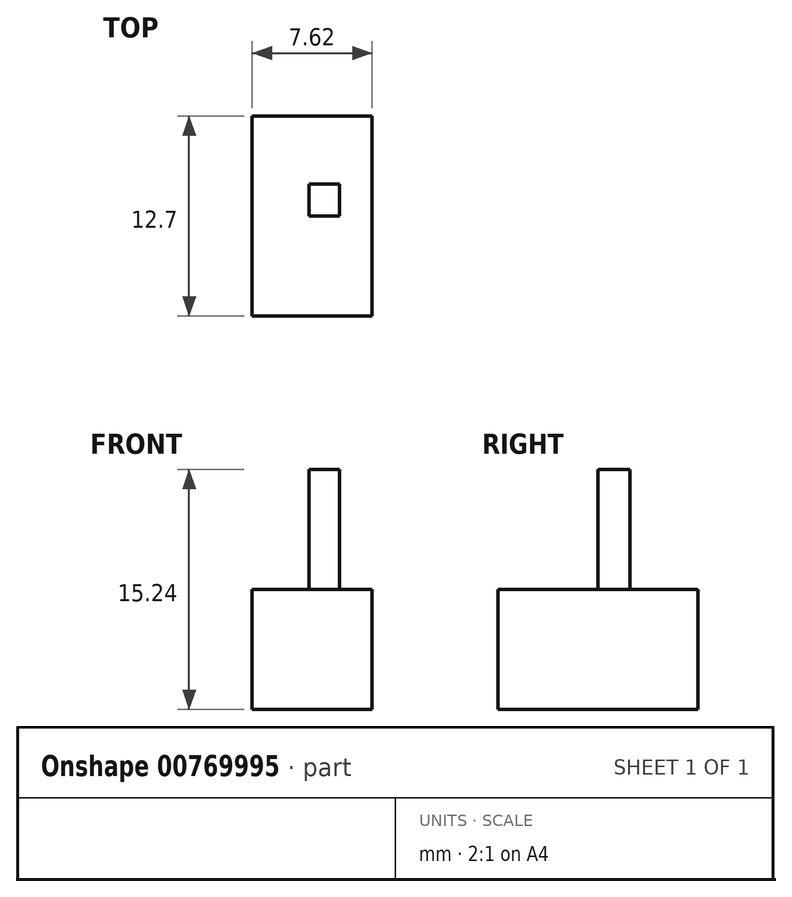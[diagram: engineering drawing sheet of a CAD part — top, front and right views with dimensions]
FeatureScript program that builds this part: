
annotation { "Feature Type Name" : "Feature", "Feature Type Description" : "" }
export const myFeature = defineFeature(function(context is Context, id is Id, definition is map)
    precondition{}
    {
        {
            var Q0;
            Q0=qCreatedBy(makeId("Top.planeOp"),FACE);
            var sketch = newSketch(context, id + "F0", { "sketchPlane" : qUnion([Q0])});
            skLineSegment(sketch, "E0.bottom", {"start": v(-56.96, -32.9) * mm, "end": v(-49.34, -32.9) * mm});
            skLineSegment(sketch, "E0.top", {"start": v(-56.96, -45.6) * mm, "end": v(-49.34, -45.6) * mm});
            skLineSegment(sketch, "E0.left", {"start": v(-56.96, -32.9) * mm, "end": v(-56.96, -45.6) * mm});
            skLineSegment(sketch, "E0.right", {"start": v(-49.34, -32.9) * mm, "end": v(-49.34, -45.6) * mm});
            skSolve(sketch);
        }
        {
            var Q0;
            Q0 = qSketchRegion(id + "F0", true);
            extrude(context, id + "F1", {"entities" : qUnion([Q0]), "depth" : 7.62 * mm, "offsetDistance" : 25.4 * mm});
        }
        {
            var Q0;
            Q0=makeQuery(id+"F1.opExtrude","CAP_FACE",FACE,{"disambiguationData":[OSD([sQuery(id+"F0.wireOp",EDGE,"E0.bottom"),sQuery(id+"F0.wireOp",EDGE,"E0.top"),sQuery(id+"F0.wireOp",EDGE,"E0.left"),sQuery(id+"F0.wireOp",EDGE,"E0.right")])],"isStart":false});
            var sketch = newSketch(context, id + "F2", { "sketchPlane" : qUnion([Q0])});
            skPoint(sketch, "E1.oppositeSnap0", {"position": v(-49.34, -39.25) * mm});
            skLineSegment(sketch, "E1.bottom", {"start": v(-53.34, -37.21) * mm, "end": v(-51.42, -37.21) * mm});
            skLineSegment(sketch, "E1.top", {"start": v(-53.34, -39.25) * mm, "end": v(-51.42, -39.25) * mm});
            skLineSegment(sketch, "E1.left", {"start": v(-53.34, -37.21) * mm, "end": v(-53.34, -39.25) * mm});
            skLineSegment(sketch, "E1.right", {"start": v(-51.42, -37.21) * mm, "end": v(-51.42, -39.25) * mm});
            skSolve(sketch);
        }
        {
            var Q0;
            Q0=makeQuery(id+"F2.imprint","IMPRINT",FACE,{"disambiguationData":[TD([[makeQuery(id+"F2.imprint","IMPRINT",EDGE,{"derivedFrom":sQuery(id+"F2.wireOp",EDGE,"E1.bottom")}),-1.0]])]});
            extrude(context, id + "F3", {"entities" : qUnion([Q0]), "operationType" : NewBodyOperationType.ADD, "depth" : 7.62 * mm, "offsetDistance" : 25.4 * mm});
        }
    });
